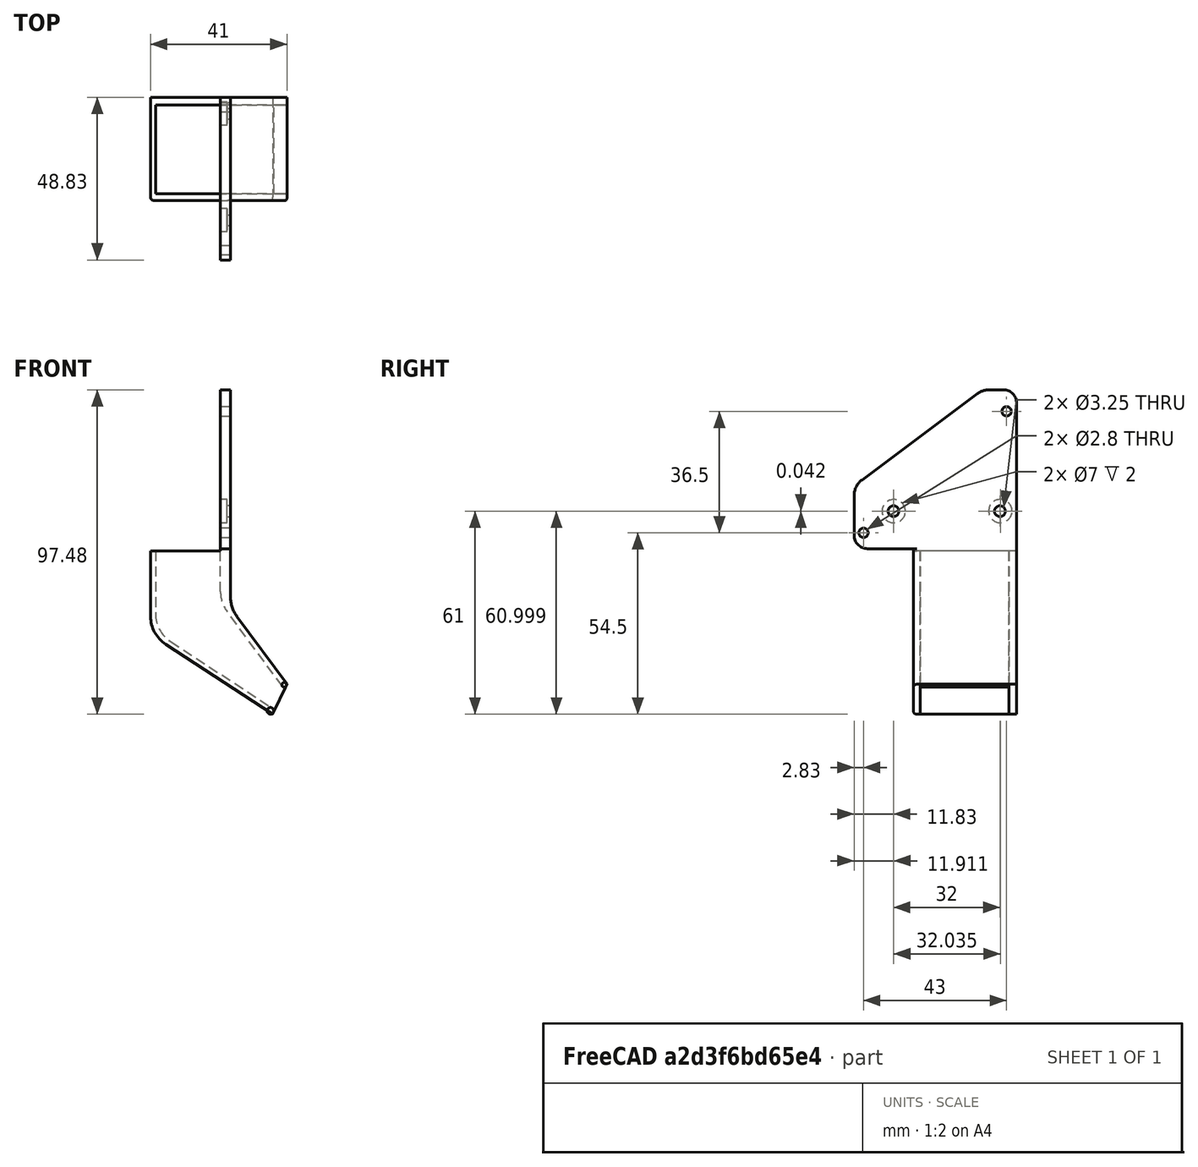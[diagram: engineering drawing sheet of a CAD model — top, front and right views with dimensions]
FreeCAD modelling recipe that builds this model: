
FCSTD DOCUMENT  (FreeCAD 0.19R)
Label: FanDuct10
License: All rights reserved
LicenseURL: http://en.wikipedia.org/wiki/All_rights_reserved
objects: Sketcher::SketchObject×9, PartDesign::Fillet×8, PartDesign::Pocket×5, PartDesign::Pad×2, PartDesign::Body×1, Mesh::Feature×1
note: 40 computed .brp shape members not serialized (recipe doc carries the construction recipe); baked Part::Feature solids carry a one-line shape summary decoded from their .brp

FEATURE [Sketcher::SketchObject] Sketch035  label="startingpos"
  FullyConstrained = false
  MapMode = 5
  Placement = pos=(-14,0,0) rot=(0.57735,-0.57735,-0.57735;2.0944rad)
  sketch-geometry (5):
    g0: Circle CenterX=35 CenterY=-20 CenterZ=0 NormalX=0 NormalY=0 NormalZ=1 AngleXU=0 Radius=1
    g1: Circle CenterX=12 CenterY=44 CenterZ=0 NormalX=0 NormalY=0 NormalZ=1 AngleXU=0 Radius=1.9
    g2: Circle CenterX=55 CenterY=44 CenterZ=0 NormalX=0 NormalY=0 NormalZ=1 AngleXU=0 Radius=1.9
    g3: LineSegment StartX=12.5 StartY=38 StartZ=0 EndX=35 EndY=38 EndZ=0
    g4: GeomPoint X=35 Y=-19 Z=0
  constraints (13):
    c: DistanceY(g0) = -20
    c: Diameter(g1) = 3.8
    c: Equal(g1,g2)
    c: DistanceY(g1) = 44
    c: DistanceX(g2) = 55
    c: DistanceY(g2) = 44
    c: Diameter(g0) = 2
    c: Horizontal(g3)
    c: Distance(g3) = 22.5
    c: DistanceX(g0) = 35
    c: DistanceX(g3) = 35
    c: DistanceY(g3) = 38
    c: DistanceX(g4) = 35
FEATURE [Sketcher::SketchObject] Sketch037  label="startingpos001"
  FullyConstrained = false
  MapMode = 5
  Placement = pos=(-35,0,2e-15) rot=(0.57735,-0.57735,-0.57735;2.0944rad)
  sketch-geometry (11):
    g0: Circle CenterX=35 CenterY=-20 CenterZ=0 NormalX=0 NormalY=0 NormalZ=1 AngleXU=0 Radius=1
    g1: Circle CenterX=12 CenterY=44 CenterZ=0 NormalX=0 NormalY=0 NormalZ=1 AngleXU=0 Radius=1.9
    g2: Circle CenterX=55 CenterY=44 CenterZ=0 NormalX=0 NormalY=0 NormalZ=1 AngleXU=0 Radius=1.9
    g3: LineSegment StartX=12.5 StartY=38 StartZ=0 EndX=35 EndY=38 EndZ=0
    g4: LineSegment StartX=5.72016 StartY=54.4932 StartZ=0 EndX=25.1498 EndY=-38.5121 EndZ=0
    g5: LineSegment StartX=25.1498 StartY=-38.5121 StartZ=0 EndX=-60.2156 EndY=-38.5121 EndZ=0
    g6: LineSegment StartX=-60.2156 StartY=-38.5121 StartZ=0 EndX=-35.1899 EndY=60.5708 EndZ=0
    g7: LineSegment StartX=-35.1899 StartY=60.5708 StartZ=0 EndX=99.6909 EndY=60.5708 EndZ=0
    g8: LineSegment StartX=56.1815 StartY=-38.9405 StartZ=0 EndX=37.0599 EndY=52.5904 EndZ=0
    g9: LineSegment StartX=56.1815 StartY=-38.9405 StartZ=0 EndX=99.6909 EndY=60.5708 EndZ=0
    g10: LineSegment StartX=5.72016 StartY=54.4932 StartZ=0 EndX=37.0599 EndY=52.5904 EndZ=0
  constraints (27):
    c: DistanceY(g0) = -20
    c: Diameter(g1) = 3.8
    c: Equal(g1,g2)
    c: DistanceX(g1) = 12
    c: DistanceY(g1) = 44
    c: DistanceX(g2) = 55
    c: DistanceY(g2) = 44
    c: Diameter(g0) = 2
    c: Horizontal(g3)
    c: Distance(g3) = 22.5
    c: DistanceX(g0) = 35
    c: DistanceX(g3) = 35
    c: DistanceY(g3) = 38
    c: Horizontal(g5)
    c: Coincident(g5,g6)
    c: Coincident(g6,g7)
    c: Horizontal(g7)
    c: Distance(g3,g8) = 5
    c: Coincident(g5,g4)
    c: Coincident(g8,g9)
    c: Coincident(g9,g7)
    c: DistanceX(g7) = 99.6909
    c: DistanceY(g7) = 60.5708
    c: DistanceX(g6) = -35.1899
    c: Parallel(g8,g4)
    c: Coincident(g10,g4)
    c: Coincident(g10,g8)
FEATURE [Sketcher::SketchObject] Sketch  label="Body001"
  FullyConstrained = true
  MapMode = 5
  Placement = pos=(0,0,0) rot=(1,0,0;1.5708rad)
  Support = -> [XZ_Plane]
  sketch-geometry (14):
    g0: LineSegment StartX=0 StartY=35 StartZ=0 EndX=-3 EndY=35 EndZ=0
    g1: LineSegment StartX=-3 StartY=35 StartZ=0 EndX=-3 EndY=-15 EndZ=0
    g2: LineSegment StartX=-3 StartY=-15 StartZ=0 EndX=-24 EndY=-15 EndZ=0
    g3: LineSegment StartX=-24 StartY=-15 StartZ=0 EndX=-24 EndY=-40 EndZ=0
    g4: GeomPoint X=25 Y=-65 Z=0
    g5: LineSegment StartX=0 StartY=0 StartZ=0 EndX=53.43 EndY=0 EndZ=0
    g6: LineSegment StartX=53.43 StartY=0 StartZ=0 EndX=53.43 EndY=-30 EndZ=0
    g7: LineSegment StartX=53.43 StartY=-30 StartZ=0 EndX=0 EndY=-30 EndZ=0
    g8: LineSegment StartX=0 StartY=-30 StartZ=0 EndX=0 EndY=0 EndZ=0
    g9: LineSegment StartX=0 StartY=0 StartZ=0 EndX=0 EndY=-32 EndZ=0
    g10: LineSegment StartX=0 StartY=-32 StartZ=0 EndX=17 EndY=-55 EndZ=0
    g11: LineSegment StartX=-24 StartY=-40 StartZ=0 EndX=12.6411 EndY=-64 EndZ=0
    g12: LineSegment StartX=12.6411 StartY=-64 StartZ=0 EndX=17 EndY=-55 EndZ=0
    g13: LineSegment StartX=0 StartY=35 StartZ=0 EndX=0 EndY=0 EndZ=0
  constraints (39):
    c: PointOnObject(g0,g-2)
    c: Coincident(g0,g1)
    c: Vertical(g1)
    c: Coincident(g1,g2)
    c: Horizontal(g2)
    c: Coincident(g2,g3)
    c: Vertical(g3)
    c: Horizontal(g0)
    c: Distance(g0) = 3
    c: DistanceX(g4) = 25
    c: DistanceY(g4) = -65
    c: Distance(g2) = 21
    c: Distance(g3) = 25
    c: DistanceY(g1) = -15
    c: Distance(g1) = 50
    c: Coincident(g5,g6)
    c: Coincident(g6,g7)
    c: Coincident(g7,g8)
    c: Coincident(g8,g5)
    c: Horizontal(g5)
    c: Horizontal(g7)
    c: Vertical(g6)
    c: Vertical(g8)
    c: DistanceY(g6) = -30
    c: Coincident(g5,g-1)
    c: Coincident(g-1,g9)
    c: Vertical(g9)
    c: Coincident(g9,g10)
    c: DistanceY(g4,g10) = 10
    c: DistanceX(g10,g4) = 8
    c: Coincident(g11,g3)
    c: DistanceY(g11,g4) = -1
    c: Distance(g11,g10) = 10
    c: Coincident(g11,g12)
    c: Coincident(g12,g10)
    c: Distance(g9,g7) = 2
    c: DistanceX(g6) = 53.43
    c: Coincident(g0,g13)
    c: Coincident(g13,g9)
FEATURE [PartDesign::Pad] Pad
  Direction = (1,1,1)
  Length = 65
  Length2 = 100
  Placement = pos=(0,0,0) rot=(1,0,0;1.5708rad)
  Profile = -> Sketch
  Type = 0
FEATURE [Sketcher::SketchObject] Sketch052  label="Mountholes"
  FullyConstrained = true
  MapMode = 5
  Placement = pos=(-3,0,0) rot=(0.707107,0,-0.707107;3.14159rad)
  Support = -> [Pad]
  sketch-geometry (2):
    g0: Circle CenterX=3 CenterY=20 CenterZ=0 NormalX=0 NormalY=0 NormalZ=1 AngleXU=0 Radius=1.625
    g1: Circle CenterX=3 CenterY=52 CenterZ=0 NormalX=0 NormalY=0 NormalZ=1 AngleXU=0 Radius=1.625
  constraints (6):
    c: Diameter(g1) = 3.25
    c: Equal(g1,g0)
    c: DistanceY(g0) = 20
    c: DistanceX(g0) = 3
    c: DistanceX(g1) = 3
    c: Distance(g0,g1) = 32
FEATURE [PartDesign::Pocket] Pocket
  BaseFeature = -> Pad
  Length = 5
  Length2 = 100
  Placement = pos=(0,0,0) rot=(1,0,0;1.5708rad)
  Profile = -> Sketch052
  Type = 0
FEATURE [Sketcher::SketchObject] Sketch062  label="outlineCut"
  ExternalGeometry = -> [Pocket]
  FullyConstrained = false
  MapMode = 5
  Placement = pos=(-3,0,0) rot=(0.707107,0,-0.707107;3.14159rad)
  Support = -> [Pocket]
  sketch-geometry (17):
    g0: LineSegment StartX=67 StartY=15 StartZ=0 EndX=14.2621 EndY=15 EndZ=0
    g1: LineSegment StartX=14.2621 StartY=15 StartZ=0 EndX=-3.25457 EndY=15 EndZ=0
    g2: LineSegment StartX=-3.25457 StartY=15 StartZ=0 EndX=-33.4784 EndY=15 EndZ=0
    g3: LineSegment StartX=-33.4784 StartY=15 StartZ=0 EndX=-33.4784 EndY=25.1764 EndZ=0
    g4: LineSegment StartX=-33.4784 StartY=25.1764 StartZ=0 EndX=-4.64227 EndY=63.8264 EndZ=0
    g5: LineSegment StartX=-4.64227 StartY=63.8264 StartZ=0 EndX=14.2621 EndY=63.8264 EndZ=0
    g6: LineSegment StartX=14.2621 StartY=63.8264 StartZ=0 EndX=14.2621 EndY=46 EndZ=0
    g7: LineSegment StartX=14.2621 StartY=46 StartZ=0 EndX=67 EndY=46 EndZ=0
    g8: LineSegment StartX=67 StartY=46 StartZ=0 EndX=67 EndY=15 EndZ=0
    g9: Circle CenterX=67 CenterY=30 CenterZ=0 NormalX=0 NormalY=0 NormalZ=1 AngleXU=0 Radius=2.43328
    g10: Circle CenterX=14.2621 CenterY=30.5 CenterZ=0 NormalX=0 NormalY=0 NormalZ=1 AngleXU=0 Radius=1.32268
    g11: LineSegment StartX=67 StartY=46 StartZ=0 EndX=69.9693 EndY=84.1734 EndZ=0
    g12: LineSegment StartX=69.9693 StartY=84.1734 StartZ=0 EndX=11.0977 EndY=87.4268 EndZ=0
    g13: LineSegment StartX=11.0977 StartY=87.4268 StartZ=0 EndX=-68.9986 EndY=87.4268 EndZ=0
    g14: LineSegment StartX=-68.9986 StartY=87.4268 StartZ=0 EndX=-68.9986 EndY=-45.6539 EndZ=0
    g15: LineSegment StartX=-68.9986 StartY=-45.6539 StartZ=0 EndX=88.0955 EndY=-45.6539 EndZ=0
    g16: LineSegment StartX=88.0955 StartY=-45.6539 StartZ=0 EndX=67 EndY=15 EndZ=0
  constraints (32):
    c: Horizontal(g1)
    c: Coincident(g1,g2)
    c: Coincident(g2,g3)
    c: Vertical(g3)
    c: Coincident(g3,g4)
    c: Coincident(g4,g5)
    c: Horizontal(g5)
    c: Coincident(g5,g6)
    c: Vertical(g6)
    c: Coincident(g6,g7)
    c: Coincident(g7,g8)
    c: Coincident(g8,g0)
    c: Vertical(g8)
    c: DistanceY(g-3,g9) = 10
    c: DistanceX(g-3,g9) = 64
    c: Distance(g8) = 31
    c: Symmetric(g0,g6,g10)
    c: Distance(g0,g6) = 31
    c: DistanceY(g0,g-3) = 5
    c: Horizontal(g0)
    c: Coincident(g7,g11)
    c: Coincident(g11,g12)
    c: Coincident(g12,g13)
    c: Horizontal(g13)
    c: Coincident(g13,g14)
    c: Vertical(g14)
    c: Coincident(g14,g15)
    c: Horizontal(g15)
    c: Coincident(g15,g16)
    c: Coincident(g16,g0)
    c: Coincident(g1,g0)
    c: Horizontal(g2)
FEATURE [PartDesign::Pocket] Pocket001
  BaseFeature = -> Pocket
  Length = 29
  Length2 = 100
  Placement = pos=(0,0,0) rot=(1,0,0;1.5708rad)
  Profile = -> Sketch062
  Type = 4
FEATURE [Sketcher::SketchObject] Sketch061  label="cavity"
  ExternalGeometry = -> [Pocket]
  FullyConstrained = true
  MapMode = 5
  Placement = pos=(0,-15,5e-15) rot=(-1,0,0;1.5708rad)
  Support = -> [Pocket001]
  sketch-geometry (6):
    g0: LineSegment StartX=-3 StartY=15 StartZ=0 EndX=-22.5 EndY=15 EndZ=0
    g1: LineSegment StartX=-22.5 StartY=15 StartZ=0 EndX=-22.5 EndY=39.1894 EndZ=0
    g2: LineSegment StartX=-3 StartY=30.4648 StartZ=0 EndX=-3 EndY=15 EndZ=0
    g3: LineSegment StartX=-22.5 StartY=39.1894 StartZ=0 EndX=14.4243 EndY=63.3749 EndZ=0
    g4: LineSegment StartX=14.4243 StartY=63.3749 StartZ=0 EndX=17.6664 EndY=58.4251 EndZ=0
    g5: LineSegment StartX=17.6664 StartY=58.4251 StartZ=0 EndX=-3 EndY=30.4648 EndZ=0
  constraints (17):
    c: Horizontal(g0)
    c: Coincident(g0,g1)
    c: Vertical(g1)
    c: Coincident(g2,g0)
    c: Vertical(g2)
    c: Coincident(g1,g3)
    c: Coincident(g3,g4)
    c: Coincident(g4,g5)
    c: Coincident(g5,g2)
    c: Distance(g2,g-3) = 1.5
    c: Distance(g-4,g3) = 1.5
    c: Distance(g-3,g5) = 1.5
    c: Distance(g1,g-4) = 1.5
    c: Distance(g1,g-5) = 1.5
    c: Coincident(g0,g-6)
    c: Perpendicular(g4,g3)
    c: Distance(g3) = 44.14
FEATURE [PartDesign::Pocket] Pocket002
  BaseFeature = -> Pocket001
  Length = 29
  Length2 = 100
  Placement = pos=(0,0,0) rot=(1,0,0;1.5708rad)
  Profile = -> Sketch061
  Type = 0
FEATURE [Sketcher::SketchObject] Sketch064  label="cap"
  FullyConstrained = false
  MapMode = 5
  Placement = pos=(0,-15,6.7e-15) rot=(-1,0,0;1.5708rad)
  Support = -> [Pocket002]
  sketch-geometry (6):
    g0: LineSegment StartX=16.2616 StartY=56.5246 StartZ=0 EndX=-2.74511 EndY=30.8096 EndZ=0
    g1: LineSegment StartX=-2.74511 StartY=30.8096 StartZ=0 EndX=-2.74511 EndY=15 EndZ=0
    g2: LineSegment StartX=-2.74511 StartY=15 StartZ=0 EndX=-22.5554 EndY=15 EndZ=0
    g3: LineSegment StartX=-22.5554 StartY=15 StartZ=0 EndX=-22.5554 EndY=39.3733 EndZ=0
    g4: LineSegment StartX=-22.5554 StartY=39.3733 StartZ=0 EndX=13.3004 EndY=62.6387 EndZ=0
    g5: LineSegment StartX=13.3004 StartY=62.6387 StartZ=0 EndX=16.2616 EndY=56.5246 EndZ=0
  constraints (9):
    c: Coincident(g0,g1)
    c: Vertical(g1)
    c: Coincident(g1,g2)
    c: Horizontal(g2)
    c: Coincident(g2,g3)
    c: Vertical(g3)
    c: Coincident(g3,g4)
    c: Coincident(g4,g5)
    c: Coincident(g5,g0)
FEATURE [PartDesign::Pad] Pad001
  BaseFeature = -> Pocket002
  Direction = (1,1,1)
  Length = 2.25
  Length2 = 100
  Placement = pos=(0,0,0) rot=(1,0,0;1.5708rad)
  Profile = -> Sketch064
  Reversed = true
  Type = 0
FEATURE [Sketcher::SketchObject] Sketch066  label="fanholes"
  FullyConstrained = true
  MapMode = 5
  Placement = pos=(-3,0,0) rot=(0.707107,0,-0.707107;3.14159rad)
  Support = -> [Pad001]
  sketch-geometry (2):
    g0: Circle CenterX=-27 CenterY=18 CenterZ=0 NormalX=0 NormalY=0 NormalZ=1 AngleXU=0 Radius=1.4
    g1: Circle CenterX=9.5 CenterY=61 CenterZ=0 NormalX=0 NormalY=0 NormalZ=1 AngleXU=0 Radius=1.4
  constraints (6):
    c: Diameter(g0) = 2.8
    c: Equal(g0,g1)
    c: DistanceX(g1) = 9.5
    c: DistanceY(g1) = 61
    c: DistanceX(g0) = -27
    c: DistanceY(g0) = 18
FEATURE [PartDesign::Pocket] Pocket003
  BaseFeature = -> Pad001
  Length = 5
  Length2 = 100
  Placement = pos=(0,0,0) rot=(1,0,0;1.5708rad)
  Profile = -> Sketch066
  Type = 0
FEATURE [Sketcher::SketchObject] Sketch068
  FullyConstrained = false
  MapMode = 5
  Placement = pos=(-3,0,0) rot=(0.707107,0,-0.707107;3.14159rad)
  sketch-geometry (2):
    g0: Circle CenterX=2.95829 CenterY=19.8839 CenterZ=0 NormalX=0 NormalY=0 NormalZ=1 AngleXU=0 Radius=3.5
    g1: Circle CenterX=3.00051 CenterY=51.9186 CenterZ=0 NormalX=0 NormalY=0 NormalZ=1 AngleXU=0 Radius=3.5
  constraints (2):
    c: Diameter(g0) = 7
    c: Equal(g0,g1)
FEATURE [PartDesign::Pocket] Pocket004
  BaseFeature = -> Pocket003
  Length = 2
  Length2 = 100
  Placement = pos=(0,0,0) rot=(1,0,0;1.5708rad)
  Profile = -> Sketch068
  Type = 0
FEATURE [PartDesign::Fillet] Fillet
  Base = -> Pocket004 [Edge24,Edge21]
  BaseFeature = -> Pocket004
  Placement = pos=(0,0,0) rot=(1,0,0;1.5708rad)
  Radius = 4
  SupportTransform = false
FEATURE [PartDesign::Fillet] Fillet001
  Base = -> Fillet [Edge29,Edge18]
  BaseFeature = -> Fillet
  Placement = pos=(0,0,0) rot=(1,0,0;1.5708rad)
  Radius = 6
  SupportTransform = false
FEATURE [PartDesign::Fillet] Fillet002
  Base = -> Fillet001 [Edge34,Edge110]
  BaseFeature = -> Fillet001
  Placement = pos=(0,0,0) rot=(1,0,0;1.5708rad)
  Radius = 10
  SupportTransform = false
FEATURE [PartDesign::Fillet] Fillet003
  Base = -> Fillet002 [Edge61,Edge107]
  BaseFeature = -> Fillet002
  Placement = pos=(0,0,0) rot=(1,0,0;1.5708rad)
  Radius = 10
  SupportTransform = false
FEATURE [PartDesign::Fillet] Fillet004
  Base = -> Fillet003 [Edge1]
  BaseFeature = -> Fillet003
  Placement = pos=(0,0,0) rot=(1,0,0;1.5708rad)
  Radius = 1
  SupportTransform = false
FEATURE [PartDesign::Fillet] Fillet005
  Base = -> Fillet004 [Edge3]
  BaseFeature = -> Fillet004
  Placement = pos=(0,0,0) rot=(1,0,0;1.5708rad)
  Radius = 1
  SupportTransform = false
FEATURE [PartDesign::Fillet] Fillet006
  Base = -> Fillet005 [Edge19]
  BaseFeature = -> Fillet005
  Placement = pos=(0,0,0) rot=(1,0,0;1.5708rad)
  Radius = 0.7
  SupportTransform = false
FEATURE [PartDesign::Fillet] Fillet007
  Base = -> Fillet006 [Edge9]
  BaseFeature = -> Fillet006
  Placement = pos=(0,0,0) rot=(1,0,0;1.5708rad)
  Radius = 1
  SupportTransform = false
FEATURE [PartDesign::Body] Body
  Group = -> [Sketch035,Sketch037,Sketch,Pad,Sketch052,Sketch061,Pocket,Sketch062,Pocket001,Sketch064,Sketch066,Pocket002,Pad001,Pocket003,Sketch068,Pocket004,Fillet,Fillet001,Fillet002,Fillet003,Fillet004,Fillet005,Fillet006,Fillet007]
  Origin = -> Origin
  Tip = -> Fillet007
FEATURE [Mesh::Feature] Mesh  label="Fillet007 (Meshed)"
